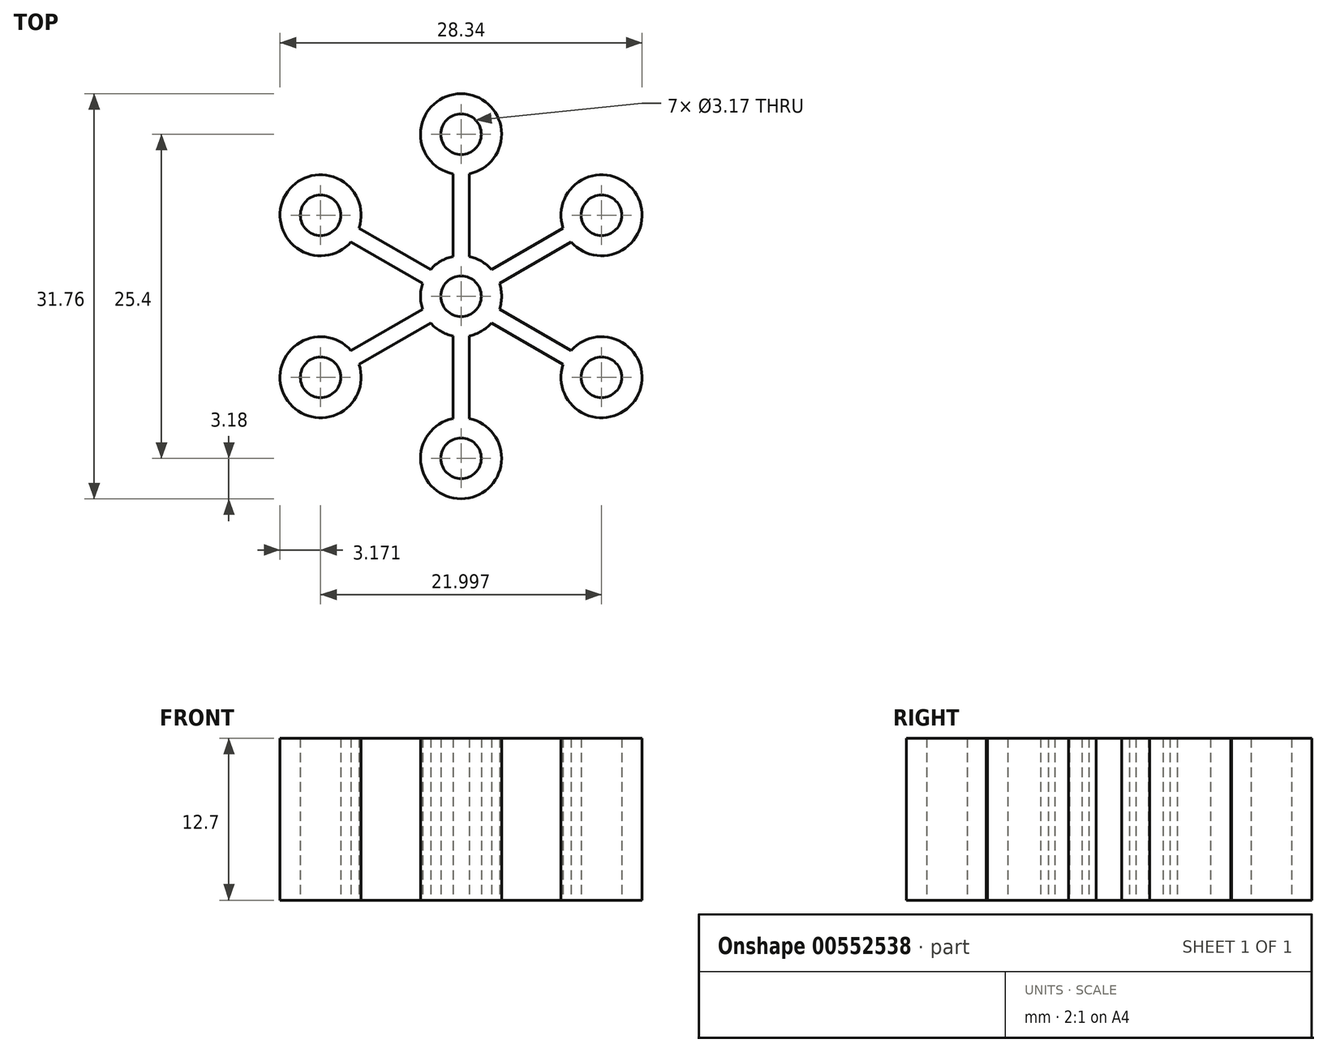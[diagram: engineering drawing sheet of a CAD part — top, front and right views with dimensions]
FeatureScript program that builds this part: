
annotation { "Feature Type Name" : "Feature", "Feature Type Description" : "" }
export const myFeature = defineFeature(function(context is Context, id is Id, definition is map)
    precondition{}
    {
        {
            var Q0;
            Q0=qCreatedBy(makeId("Top.planeOp"),FACE);
            var sketch = newSketch(context, id + "F0", { "sketchPlane" : qUnion([Q0])});
            skCircle(sketch, "E0", {"center": v(0, 0) * mm, "radius": 12.7 * mm, "construction": true});
            skCircle(sketch, "E1", {"center": v(0, 0) * mm, "radius": 3.18 * mm});
            skLineSegment(sketch, "E2", {"start": v(0, 0) * mm, "end": v(0, 12.7) * mm, "construction": true});
            skLineSegment(sketch, "E3", {"start": v(0, 0) * mm, "end": v(11, 6.35) * mm, "construction": true});
            skLineSegment(sketch, "E4", {"start": v(0, 0) * mm, "end": v(11, -6.35) * mm, "construction": true});
            skLineSegment(sketch, "E5", {"start": v(0, 0) * mm, "end": v(0, -12.7) * mm, "construction": true});
            skLineSegment(sketch, "E6", {"start": v(0, 0) * mm, "end": v(-11, -6.35) * mm, "construction": true});
            skLineSegment(sketch, "E7", {"start": v(0, 0) * mm, "end": v(-11, 6.35) * mm, "construction": true});
            skCircle(sketch, "E8", {"center": v(0, 12.7) * mm, "radius": 3.17 * mm});
            skCircle(sketch, "E9", {"center": v(11, 6.35) * mm, "radius": 3.18 * mm});
            skCircle(sketch, "E10", {"center": v(11, -6.35) * mm, "radius": 3.18 * mm});
            skCircle(sketch, "E11", {"center": v(0, -12.7) * mm, "radius": 3.18 * mm});
            skCircle(sketch, "E12", {"center": v(-11, -6.35) * mm, "radius": 3.18 * mm});
            skCircle(sketch, "E13", {"center": v(-11, 6.35) * mm, "radius": 3.18 * mm});
            skLineSegment(sketch, "E14", {"start": v(-0.64, 9.59) * mm, "end": v(-0.63, 3.11) * mm});
            skLineSegment(sketch, "E15.MirrorCS", {"start": v(0.63, 9.59) * mm, "end": v(0.64, 3.11) * mm});
            skLineSegment(sketch, "E16.MirrorCS", {"start": v(-0.63, -9.59) * mm, "end": v(-0.63, -3.11) * mm});
            skLineSegment(sketch, "E17.MirrorCS", {"start": v(0.64, -9.59) * mm, "end": v(0.64, -3.11) * mm});
            skLineSegment(sketch, "E18", {"start": v(7.99, 5.34) * mm, "end": v(2.38, 2.1) * mm});
            skLineSegment(sketch, "E19.MirrorCS", {"start": v(8.62, 4.24) * mm, "end": v(3.01, 1) * mm});
            skLineSegment(sketch, "E20.MirrorCS", {"start": v(-8.62, 4.24) * mm, "end": v(-3.01, 1) * mm});
            skLineSegment(sketch, "E21.MirrorCS", {"start": v(-7.99, 5.34) * mm, "end": v(-2.38, 2.1) * mm});
            skLineSegment(sketch, "E22", {"start": v(-1.59, 2.75) * mm, "end": v(0, 0) * mm, "construction": true});
            skLineSegment(sketch, "E23.MirrorCS", {"start": v(-8.62, -4.24) * mm, "end": v(-3.01, -1) * mm});
            skLineSegment(sketch, "E24.MirrorCS", {"start": v(-7.99, -5.34) * mm, "end": v(-2.38, -2.1) * mm});
            skLineSegment(sketch, "E25.MirrorCS", {"start": v(7.99, -5.34) * mm, "end": v(2.38, -2.1) * mm});
            skLineSegment(sketch, "E26.MirrorCS", {"start": v(8.62, -4.24) * mm, "end": v(3.01, -1) * mm});
            skCircle(sketch, "E27", {"center": v(0, 0) * mm, "radius": 1.59 * mm});
            skCircle(sketch, "E28", {"center": v(-11, 6.35) * mm, "radius": 1.59 * mm});
            skCircle(sketch, "E29", {"center": v(0, -12.7) * mm, "radius": 1.59 * mm});
            skCircle(sketch, "E30", {"center": v(11, -6.35) * mm, "radius": 1.59 * mm});
            skCircle(sketch, "E31", {"center": v(-11, -6.35) * mm, "radius": 1.59 * mm});
            skCircle(sketch, "E32", {"center": v(11, 6.35) * mm, "radius": 1.59 * mm});
            skCircle(sketch, "E33", {"center": v(0, 12.7) * mm, "radius": 1.59 * mm});
            skSolve(sketch);
        }
        {
            var Q0;
            Q0 = qSketchRegion(id + "F0", true);
            extrude(context, id + "F1", {"entities" : qUnion([Q0]), "depth" : 12.7 * mm, "offsetDistance" : 25.4 * mm});
        }
    });
